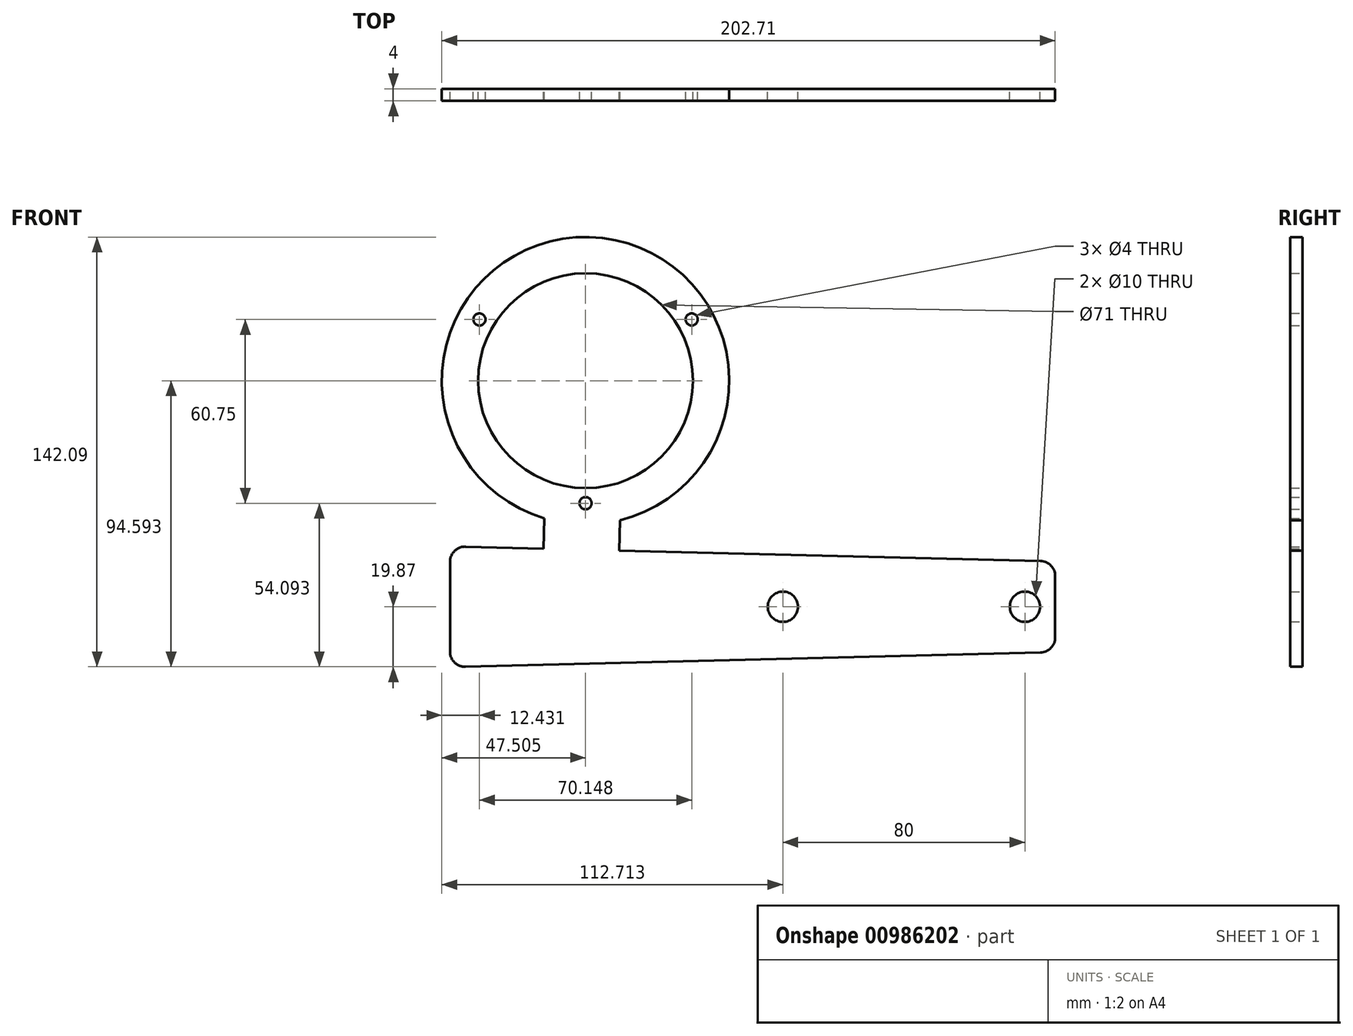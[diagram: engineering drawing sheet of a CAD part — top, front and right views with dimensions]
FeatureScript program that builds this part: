
annotation { "Feature Type Name" : "Feature", "Feature Type Description" : "" }
export const myFeature = defineFeature(function(context is Context, id is Id, definition is map)
    precondition{}
    {
        {
            var Q0;
            Q0=qCreatedBy(makeId("Front.planeOp"),FACE);
            var sketch = newSketch(context, id + "F0", { "sketchPlane" : qUnion([Q0])});
            skLineSegment(sketch, "E0", {"start": v(-74.77, 0) * mm, "end": v(125.23, 0) * mm, "construction": true});
            skLineSegment(sketch, "E1", {"start": v(-74.77, 0) * mm, "end": v(-74.77, 40) * mm, "construction": true});
            skLineSegment(sketch, "E2", {"start": v(-74.77, 40) * mm, "end": v(125.23, 40) * mm, "construction": true});
            skLineSegment(sketch, "E3", {"start": v(125.23, 40) * mm, "end": v(125.23, 0) * mm, "construction": true});
            skLineSegment(sketch, "E4", {"start": v(-74.77, 34.87) * mm, "end": v(-74.77, 5.13) * mm});
            skLineSegment(sketch, "E5", {"start": v(-69.64, 0.13) * mm, "end": v(120.36, 4.88) * mm});
            skLineSegment(sketch, "E6", {"start": v(-69.64, 39.87) * mm, "end": v(-43.87, 39.23) * mm});
            skLineSegment(sketch, "E7", {"start": v(125.23, 30.12) * mm, "end": v(125.23, 9.88) * mm});
            skPoint(sketch, "E8.visualSharp", {"position": v(-74.77, 40) * mm});
            skArc(sketch, "E8.filletArc", {"start": v(-69.64, 39.87) * mm, "mid": v(-73.26, 38.45) * mm, "end": v(-74.77, 34.87) * mm});
            skPoint(sketch, "E9.visualSharp", {"position": v(-74.77, 0) * mm});
            skArc(sketch, "E9.filletArc", {"start": v(-74.77, 5.13) * mm, "mid": v(-73.26, 1.55) * mm, "end": v(-69.64, 0.13) * mm});
            skPoint(sketch, "E10.visualSharp", {"position": v(125.23, 35) * mm});
            skArc(sketch, "E10.filletArc", {"start": v(125.23, 30.12) * mm, "mid": v(123.81, 33.61) * mm, "end": v(120.36, 35.12) * mm});
            skPoint(sketch, "E11.visualSharp", {"position": v(125.23, 5) * mm});
            skArc(sketch, "E11.filletArc", {"start": v(120.36, 4.88) * mm, "mid": v(123.81, 6.39) * mm, "end": v(125.23, 9.88) * mm});
            skLineSegment(sketch, "E12", {"start": v(25.23, 40) * mm, "end": v(25.23, 0) * mm, "construction": true});
            skLineSegment(sketch, "E13", {"start": v(-43.87, 39.23) * mm, "end": v(-43.62, 49.22) * mm});
            skLineSegment(sketch, "E14", {"start": v(-18.87, 38.6) * mm, "end": v(-18.62, 48.6) * mm});
            skLineSegment(sketch, "E15", {"start": v(-31.12, 48.91) * mm, "end": v(-28.62, 148.88) * mm, "construction": true});
            skArc(sketch, "E16", {"start": v(-18.62, 48.6) * mm, "mid": v(-28.79, 142.2) * mm, "end": v(-43.62, 49.22) * mm});
            skLineSegment(sketch, "E17.trimOffspring", {"start": v(-18.87, 38.6) * mm, "end": v(120.36, 35.12) * mm});
            skCircle(sketch, "E18", {"center": v(-29.98, 94.72) * mm, "radius": 35.5 * mm});
            skCircle(sketch, "E19", {"center": v(115.23, 20) * mm, "radius": 5 * mm});
            skCircle(sketch, "E20", {"center": v(35.23, 20) * mm, "radius": 5 * mm});
            skLineSegment(sketch, "E21", {"start": v(-29.98, 94.72) * mm, "end": v(17.52, 94.72) * mm, "construction": true});
            skLineSegment(sketch, "E22", {"start": v(-29.98, 94.72) * mm, "end": v(-77.48, 94.72) * mm, "construction": true});
            skLineSegment(sketch, "E23", {"start": v(-71.11, 94.72) * mm, "end": v(-71.11, 118.47) * mm, "construction": true});
            skLineSegment(sketch, "E24", {"start": v(-71.11, 118.47) * mm, "end": v(-29.98, 94.72) * mm, "construction": true});
            skCircle(sketch, "E25", {"center": v(-65.05, 114.97) * mm, "radius": 2 * mm});
            skLineSegment(sketch, "E26", {"start": v(11.16, 94.72) * mm, "end": v(11.16, 118.47) * mm, "construction": true});
            skLineSegment(sketch, "E27", {"start": v(11.16, 118.47) * mm, "end": v(-29.98, 94.72) * mm, "construction": true});
            skCircle(sketch, "E28", {"center": v(5.1, 114.97) * mm, "radius": 2 * mm});
            skLineSegment(sketch, "E29", {"start": v(-29.98, 40) * mm, "end": v(-29.98, 94.72) * mm, "construction": true});
            skCircle(sketch, "E30", {"center": v(-29.98, 54.22) * mm, "radius": 2 * mm});
            skSolve(sketch);
        }
        {
            var Q0;
            Q0=makeQuery(id+"F0.imprint","IMPRINT",FACE,{"disambiguationData":[TD([[makeQuery(id+"F0.imprint","IMPRINT",EDGE,{"derivedFrom":sQuery(id+"F0.wireOp",EDGE,"E4")}),1.0]])]});
            extrude(context, id + "F1", {"entities" : qUnion([Q0]), "depth" : 4 * mm, "offsetDistance" : 25 * mm});
        }
    });
